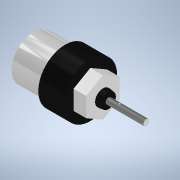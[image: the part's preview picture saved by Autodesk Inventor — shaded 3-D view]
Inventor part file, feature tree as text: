
AUTODESK INVENTOR PART (.ipt)
format: ipt  version: 2021 (Build 250183000, 183)  size: 153,600 bytes
history: native  units: mm
features: extrude x8, sketch x8
ambient origin geometry x8: Origin, YZ Plane, XZ Plane, XY Plane, X Axis, Y Axis, Z Axis, Center Point
bodies: Solid1 (feature_tree)
feature tree (16):
  extrude  "Extrusion1"  Depth=50.0mm TaperAngle=0.0deg
  extrude  "Extrusion2"  Depth=40.0mm TaperAngle=0.0deg
  extrude  "Extrusion3"  Depth=25.0mm
  extrude  "Extrusion4"  Depth=3.0mm TaperAngle=0.0deg
  extrude  "Extrusion5"  Depth=9.5mm
  extrude  "Extrusion6"  Depth=2.5mm
  extrude  "Extrusion7"  [1 undecoded]
  extrude  "Extrusion8"  [1 undecoded]
  sketch  "Sketch1"  dims[d0=70.0mm d1=50.0mm d2=0.0mm]
  sketch  "Sketch2"  dims[d3=85.0mm d4=40.0mm d5=0.0mm]
  sketch  "Sketch3"  dims[d6=20.0mm d7=0.0mm d8=25.0mm]
  sketch  "Sketch4"  dims[d9=3.0mm d10=0.0mm d11=3.0mm d12=0.0mm]
  sketch  "Sketch5"  dims[d13=3.0mm d14=0.0mm d16=9.5mm]
  sketch  "Sketch6"  dims[d17=60.0mm d18=0.0mm d19=2.5mm]
  sketch  "Sketch7"  dims[d20=20.0mm d21=0.0mm]
  sketch  "Sketch8"
note: 2 required parameter values undecoded (feature->parameter linkage not recoverable at this tier; creation-order binding heuristic only, values carry confidence <= 0.55)
